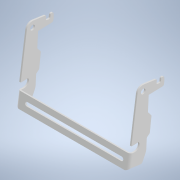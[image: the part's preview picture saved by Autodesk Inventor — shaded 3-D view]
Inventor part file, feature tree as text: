
AUTODESK INVENTOR PART (.ipt)
format: ipt  version: 2022 (Build 260153000, 153)  size: 384,000 bytes
history: native  units: mm
features: other x9, sketch x3, mirror x1
ambient origin geometry x8: Origin, YZ Plane, XZ Plane, XY Plane, X Axis, Y Axis, Z Axis, Center Point
bodies: Body1 (feature_tree)
feature tree (13):
  other  "Твердое тело1"
  other  "Грань1"
  other  "Фланец1"
  mirror  "Зеркальное отражение1"
  sketch  "Эскиз1"
  other  "Пластина1"
  sketch  "Эскиз2"
  other  "Пластина2"
  other  "Сгиб1"
  other  "УглСтык1"
  sketch  "Эскиз3"
  other  "Вырез1"
  other  "Определение1"
